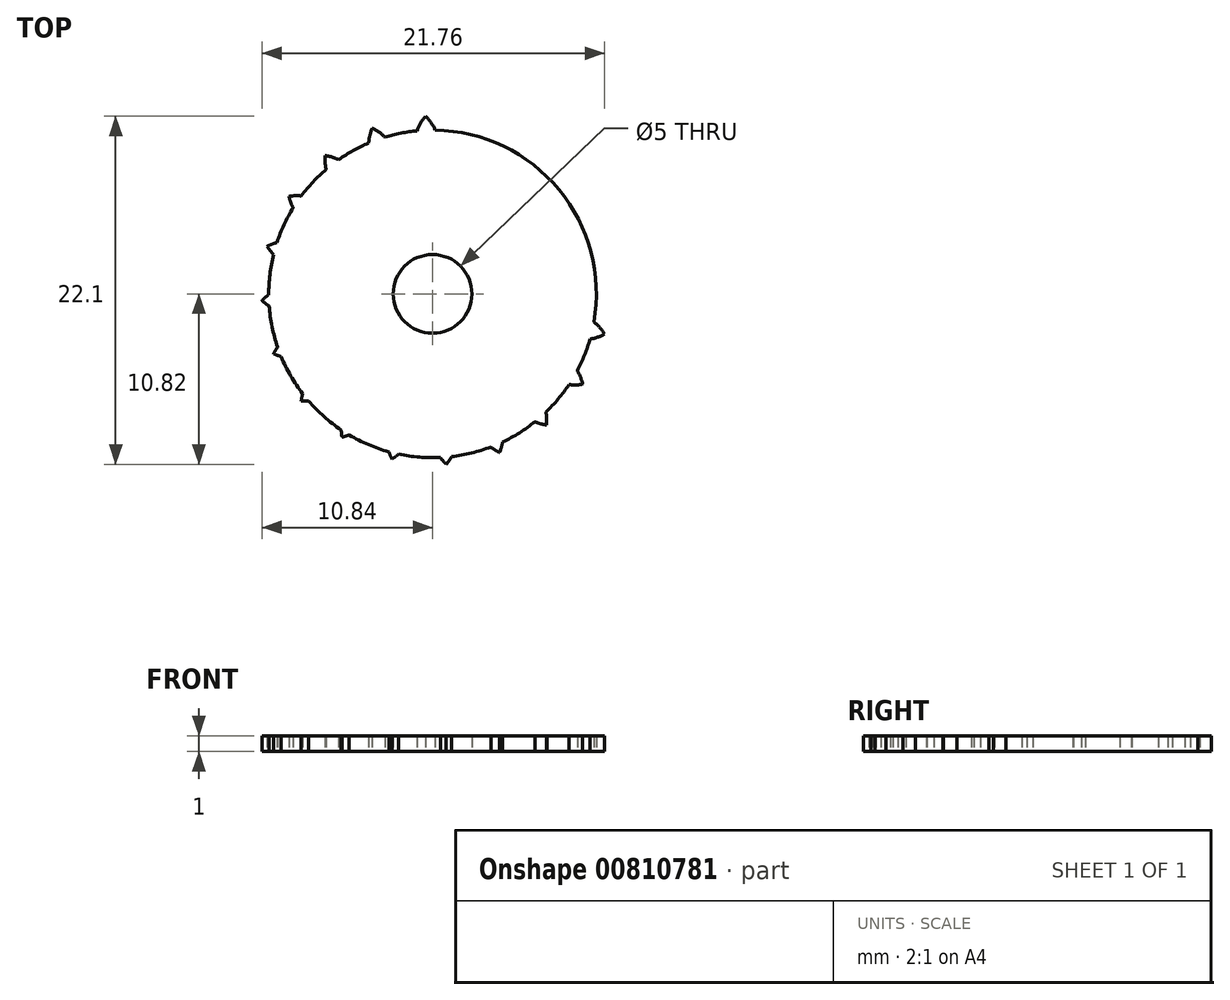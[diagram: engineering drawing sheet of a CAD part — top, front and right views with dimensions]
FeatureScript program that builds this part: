
annotation { "Feature Type Name" : "Feature", "Feature Type Description" : "" }
export const myFeature = defineFeature(function(context is Context, id is Id, definition is map)
    precondition{}
    {
        {
            assignVariable(context, id + "F0", {"name" : "GearDepth", "anyValue" : 1});
        }
        {
            var Q0;
            Q0=qCreatedBy(makeId("Top.planeOp"),FACE);
            var sketch = newSketch(context, id + "F1", { "sketchPlane" : qUnion([Q0])});
            skCircle(sketch, "E0", {"center": v(0, 0) * mm, "radius": 10.4 * mm});
            skCircle(sketch, "E1", {"center": v(0, 0) * mm, "radius": 10.95 * mm, "construction": true});
            skCircle(sketch, "E2", {"center": v(0, 0) * mm, "radius": 11.5 * mm, "construction": true});
            skLineSegment(sketch, "E3", {"start": v(0, 0) * mm, "end": v(0, 17.6) * mm, "construction": true});
            skLineSegment(sketch, "E4", {"start": v(0, 0) * mm, "end": v(-0.7, 18.04) * mm, "construction": true});
            skLineSegment(sketch, "E5", {"start": v(0, 10.95) * mm, "end": v(-10.54, 10.95) * mm, "construction": true});
            skLineSegment(sketch, "E6", {"start": v(0, 10.95) * mm, "end": v(-10.3, 7.2) * mm, "construction": true});
            skCircle(sketch, "E7", {"center": v(0, 10.95) * mm, "radius": 2.74 * mm, "construction": true});
            skCircle(sketch, "E8", {"center": v(-2.57, 10.02) * mm, "radius": 2.74 * mm, "construction": true});
            skArc(sketch, "E9", {"start": v(-5.15, 10.95) * mm, "mid": v(-5.25, 10.58) * mm, "end": v(-5.3, 10.2) * mm});
            skArc(sketch, "E10.trimOffspring", {"start": v(0.17, 10.4) * mm, "mid": v(-0.18, 11) * mm, "end": v(-0.68, 11.48) * mm});
            skArc(sketch, "E11.MirrorCS", {"start": v(-0.99, 10.36) * mm, "mid": v(-0.68, 10.98) * mm, "end": v(-0.22, 11.5) * mm});
            skLineSegment(sketch, "E12", {"start": v(-0.68, 11.48) * mm, "end": v(-0.22, 11.5) * mm});
            skArc(sketch, "E13.1.0", {"start": v(-2.97, 9.9) * mm, "mid": v(-3.5, 10.35) * mm, "end": v(-4.11, 10.65) * mm});
            skLineSegment(sketch, "E13.1.1", {"start": v(-4.11, 10.65) * mm, "end": v(-3.68, 10.81) * mm});
            skArc(sketch, "E13.1.2", {"start": v(-4.06, 9.5) * mm, "mid": v(-3.96, 10.18) * mm, "end": v(-3.68, 10.81) * mm});
            skArc(sketch, "E13.2.0", {"start": v(-5.8, 8.44) * mm, "mid": v(-6.44, 8.7) * mm, "end": v(-7.12, 8.8) * mm});
            skLineSegment(sketch, "E13.2.1", {"start": v(-7.12, 8.8) * mm, "end": v(-6.76, 9.1) * mm});
            skArc(sketch, "E13.2.2", {"start": v(-6.7, 7.72) * mm, "mid": v(-6.83, 8.4) * mm, "end": v(-6.76, 9.1) * mm});
            skArc(sketch, "E13.3.0", {"start": v(-8.04, 6.17) * mm, "mid": v(-8.73, 6.24) * mm, "end": v(-9.41, 6.12) * mm});
            skLineSegment(sketch, "E13.3.1", {"start": v(-9.41, 6.12) * mm, "end": v(-9.16, 6.5) * mm});
            skArc(sketch, "E13.3.2", {"start": v(-8.69, 5.21) * mm, "mid": v(-9, 5.83) * mm, "end": v(-9.16, 6.5) * mm});
            skArc(sketch, "E13.4.0", {"start": v(-9.48, 3.33) * mm, "mid": v(-10.15, 3.18) * mm, "end": v(-10.76, 2.86) * mm});
            skLineSegment(sketch, "E13.4.1", {"start": v(-10.76, 2.86) * mm, "end": v(-10.64, 3.3) * mm});
            skArc(sketch, "E13.4.2", {"start": v(-9.8, 2.22) * mm, "mid": v(-10.29, 2.7) * mm, "end": v(-10.64, 3.3) * mm});
            skArc(sketch, "E13.5.0", {"start": v(-9.96, 0.19) * mm, "mid": v(-10.56, -0.17) * mm, "end": v(-11.04, -0.66) * mm});
            skLineSegment(sketch, "E13.5.1", {"start": v(-11.04, -0.66) * mm, "end": v(-11.06, -0.2) * mm});
            skArc(sketch, "E13.5.2", {"start": v(-9.92, -0.97) * mm, "mid": v(-10.54, -0.66) * mm, "end": v(-11.06, -0.2) * mm});
            skArc(sketch, "E13.6.0", {"start": v(-9.45, -2.96) * mm, "mid": v(-9.9, -3.48) * mm, "end": v(-10.21, -4.1) * mm});
            skLineSegment(sketch, "E13.6.1", {"start": v(-10.21, -4.1) * mm, "end": v(-10.37, -3.66) * mm});
            skArc(sketch, "E13.6.2", {"start": v(-9.05, -4.04) * mm, "mid": v(-9.74, -3.94) * mm, "end": v(-10.37, -3.66) * mm});
            skArc(sketch, "E13.7.0", {"start": v(-8, -5.79) * mm, "mid": v(-8.27, -6.42) * mm, "end": v(-8.36, -7.1) * mm});
            skLineSegment(sketch, "E13.7.1", {"start": v(-8.36, -7.1) * mm, "end": v(-8.65, -6.74) * mm});
            skArc(sketch, "E13.7.2", {"start": v(-7.28, -6.7) * mm, "mid": v(-7.96, -6.8) * mm, "end": v(-8.65, -6.74) * mm});
            skArc(sketch, "E13.8.0", {"start": v(-5.73, -8.03) * mm, "mid": v(-5.8, -8.72) * mm, "end": v(-5.68, -9.4) * mm});
            skLineSegment(sketch, "E13.8.1", {"start": v(-5.68, -9.4) * mm, "end": v(-6.06, -9.14) * mm});
            skArc(sketch, "E13.8.2", {"start": v(-4.77, -8.67) * mm, "mid": v(-5.38, -9) * mm, "end": v(-6.06, -9.14) * mm});
            skArc(sketch, "E13.9.0", {"start": v(-2.9, -9.46) * mm, "mid": v(-2.74, -10.13) * mm, "end": v(-2.41, -10.75) * mm});
            skLineSegment(sketch, "E13.9.1", {"start": v(-2.41, -10.75) * mm, "end": v(-2.86, -10.62) * mm});
            skArc(sketch, "E13.9.2", {"start": v(-1.78, -9.77) * mm, "mid": v(-2.26, -10.27) * mm, "end": v(-2.86, -10.62) * mm});
            skArc(sketch, "E13.10.0", {"start": v(0.26, -9.94) * mm, "mid": v(0.6, -10.54) * mm, "end": v(1.1, -11.02) * mm});
            skLineSegment(sketch, "E13.10.1", {"start": v(1.1, -11.02) * mm, "end": v(0.65, -11.04) * mm});
            skArc(sketch, "E13.10.2", {"start": v(1.4, -9.9) * mm, "mid": v(1.1, -10.52) * mm, "end": v(0.65, -11.04) * mm});
            skArc(sketch, "E13.11.0", {"start": v(3.4, -9.43) * mm, "mid": v(3.92, -9.89) * mm, "end": v(4.54, -10.2) * mm});
            skLineSegment(sketch, "E13.11.1", {"start": v(4.54, -10.2) * mm, "end": v(4.1, -10.35) * mm});
            skArc(sketch, "E13.11.2", {"start": v(4.48, -9.03) * mm, "mid": v(4.38, -9.72) * mm, "end": v(4.1, -10.35) * mm});
            skArc(sketch, "E13.12.0", {"start": v(6.23, -7.98) * mm, "mid": v(6.86, -8.25) * mm, "end": v(7.55, -8.35) * mm});
            skLineSegment(sketch, "E13.12.1", {"start": v(7.55, -8.35) * mm, "end": v(7.19, -8.63) * mm});
            skArc(sketch, "E13.12.2", {"start": v(7.13, -7.26) * mm, "mid": v(7.25, -7.94) * mm, "end": v(7.19, -8.63) * mm});
            skArc(sketch, "E13.13.0", {"start": v(8.47, -5.72) * mm, "mid": v(9.16, -5.78) * mm, "end": v(9.84, -5.66) * mm});
            skLineSegment(sketch, "E13.13.1", {"start": v(9.84, -5.66) * mm, "end": v(9.58, -6.04) * mm});
            skArc(sketch, "E13.13.2", {"start": v(9.11, -4.75) * mm, "mid": v(9.43, -5.37) * mm, "end": v(9.58, -6.04) * mm});
            skArc(sketch, "E13.14.0", {"start": v(9.9, -2.87) * mm, "mid": v(10.58, -2.72) * mm, "end": v(11.19, -2.4) * mm});
            skLineSegment(sketch, "E13.14.1", {"start": v(11.19, -2.4) * mm, "end": v(11.06, -2.84) * mm});
            skArc(sketch, "E13.14.2", {"start": v(10.21, -1.76) * mm, "mid": v(10.71, -2.24) * mm, "end": v(11.06, -2.84) * mm});
            skArc(sketch, "E13.15.0", {"start": v(10.39, 0.27) * mm, "mid": v(10.98, 0.63) * mm, "end": v(11.46, 1.12) * mm});
            skLineSegment(sketch, "E13.15.1", {"start": v(11.46, 1.12) * mm, "end": v(11.48, 0.66) * mm});
            skArc(sketch, "E13.15.2", {"start": v(10.34, 1.43) * mm, "mid": v(10.96, 1.12) * mm, "end": v(11.48, 0.66) * mm});
            skArc(sketch, "E13.16.0", {"start": v(9.87, 3.41) * mm, "mid": v(10.33, 3.93) * mm, "end": v(10.64, 4.56) * mm});
            skLineSegment(sketch, "E13.16.1", {"start": v(10.64, 4.56) * mm, "end": v(10.8, 4.12) * mm});
            skArc(sketch, "E13.16.2", {"start": v(9.47, 4.5) * mm, "mid": v(10.16, 4.4) * mm, "end": v(10.8, 4.12) * mm});
            skArc(sketch, "E13.17.0", {"start": v(8.42, 6.24) * mm, "mid": v(8.7, 6.88) * mm, "end": v(8.79, 7.57) * mm});
            skLineSegment(sketch, "E13.17.1", {"start": v(8.79, 7.57) * mm, "end": v(9.07, 7.2) * mm});
            skArc(sketch, "E13.17.2", {"start": v(7.7, 7.15) * mm, "mid": v(8.38, 7.27) * mm, "end": v(9.07, 7.2) * mm});
            skArc(sketch, "E13.18.0", {"start": v(6.16, 8.49) * mm, "mid": v(6.22, 9.17) * mm, "end": v(6.1, 9.86) * mm});
            skLineSegment(sketch, "E13.18.1", {"start": v(6.1, 9.86) * mm, "end": v(6.49, 9.6) * mm});
            skArc(sketch, "E13.18.2", {"start": v(5.2, 9.13) * mm, "mid": v(5.8, 9.45) * mm, "end": v(6.49, 9.6) * mm});
            skArc(sketch, "E13.19.0", {"start": v(3.32, 9.92) * mm, "mid": v(3.16, 10.6) * mm, "end": v(2.84, 11.2) * mm});
            skLineSegment(sketch, "E13.19.1", {"start": v(2.84, 11.2) * mm, "end": v(3.28, 11.08) * mm});
            skArc(sketch, "E13.19.2", {"start": v(2.2, 10.23) * mm, "mid": v(2.69, 10.73) * mm, "end": v(3.28, 11.08) * mm});
            skPoint(sketch, "E13.center", {"position": v(0.21, 0.23) * mm});
            skCircle(sketch, "E14", {"center": v(0, 0) * mm, "radius": 2.5 * mm});
            skSolve(sketch);
        }
        {
            var Q0;
            {var subQ0=sQuery(id+"F1.wireOp",EDGE,"E10.trimOffspring");Q0=makeQuery(id+"F1.imprint","IMPRINT",FACE,{"disambiguationData":[TD([[makeQuery(id+"F1.imprint","IMPRINT",EDGE,{"derivedFrom":subQ0}),1.0]])]});}
            var Q1;
            {var subQ0=sQuery(id+"F1.wireOp",EDGE,"E0");var subQ1=makeQuery(id+"F1.imprint","INTERSECT",VERTEX,{"derivedFrom":[subQ0,sQuery(id+"F1.wireOp",EDGE,"E10.trimOffspring")]});Q1=makeQuery(id+"F1.imprint","IMPRINT",FACE,{"disambiguationData":[TD([[makeQuery(id+"F1.imprint","IMPRINT",EDGE,{"disambiguationData":[TD([[subQ1,-1.0]])],"derivedFrom":subQ0}),1.0]])]});}
            var Q2;
            {var subQ0=sQuery(id+"F1.wireOp",EDGE,"E13.1.0");Q2=makeQuery(id+"F1.imprint","IMPRINT",FACE,{"disambiguationData":[TD([[makeQuery(id+"F1.imprint","IMPRINT",EDGE,{"derivedFrom":subQ0}),1.0]])]});}
            var Q3;
            {var subQ0=sQuery(id+"F1.wireOp",EDGE,"E13.2.0");Q3=makeQuery(id+"F1.imprint","IMPRINT",FACE,{"disambiguationData":[TD([[makeQuery(id+"F1.imprint","IMPRINT",EDGE,{"derivedFrom":subQ0}),1.0]])]});}
            var Q4;
            {var subQ0=sQuery(id+"F1.wireOp",EDGE,"E13.3.0");Q4=makeQuery(id+"F1.imprint","IMPRINT",FACE,{"disambiguationData":[TD([[makeQuery(id+"F1.imprint","IMPRINT",EDGE,{"derivedFrom":subQ0}),1.0]])]});}
            var Q5;
            {var subQ0=sQuery(id+"F1.wireOp",EDGE,"E13.4.0");Q5=makeQuery(id+"F1.imprint","IMPRINT",FACE,{"disambiguationData":[TD([[makeQuery(id+"F1.imprint","IMPRINT",EDGE,{"derivedFrom":subQ0}),1.0]])]});}
            var Q6;
            {var subQ0=sQuery(id+"F1.wireOp",EDGE,"E13.5.0");Q6=makeQuery(id+"F1.imprint","IMPRINT",FACE,{"disambiguationData":[TD([[makeQuery(id+"F1.imprint","IMPRINT",EDGE,{"derivedFrom":subQ0}),1.0]])]});}
            var Q7;
            {var subQ0=sQuery(id+"F1.wireOp",EDGE,"E13.6.0");Q7=makeQuery(id+"F1.imprint","IMPRINT",FACE,{"disambiguationData":[TD([[makeQuery(id+"F1.imprint","IMPRINT",EDGE,{"derivedFrom":subQ0}),1.0]])]});}
            var Q8;
            {var subQ0=sQuery(id+"F1.wireOp",EDGE,"E13.7.0");Q8=makeQuery(id+"F1.imprint","IMPRINT",FACE,{"disambiguationData":[TD([[makeQuery(id+"F1.imprint","IMPRINT",EDGE,{"derivedFrom":subQ0}),1.0]])]});}
            var Q9;
            {var subQ0=sQuery(id+"F1.wireOp",EDGE,"E13.8.0");Q9=makeQuery(id+"F1.imprint","IMPRINT",FACE,{"disambiguationData":[TD([[makeQuery(id+"F1.imprint","IMPRINT",EDGE,{"derivedFrom":subQ0}),1.0]])]});}
            var Q10;
            {var subQ0=sQuery(id+"F1.wireOp",EDGE,"E13.9.0");Q10=makeQuery(id+"F1.imprint","IMPRINT",FACE,{"disambiguationData":[TD([[makeQuery(id+"F1.imprint","IMPRINT",EDGE,{"derivedFrom":subQ0}),1.0]])]});}
            var Q11;
            {var subQ0=sQuery(id+"F1.wireOp",EDGE,"E13.10.0");Q11=makeQuery(id+"F1.imprint","IMPRINT",FACE,{"disambiguationData":[TD([[makeQuery(id+"F1.imprint","IMPRINT",EDGE,{"derivedFrom":subQ0}),1.0]])]});}
            var Q12;
            {var subQ0=sQuery(id+"F1.wireOp",EDGE,"E13.11.0");Q12=makeQuery(id+"F1.imprint","IMPRINT",FACE,{"disambiguationData":[TD([[makeQuery(id+"F1.imprint","IMPRINT",EDGE,{"derivedFrom":subQ0}),1.0]])]});}
            var Q13;
            {var subQ0=sQuery(id+"F1.wireOp",EDGE,"E13.12.0");Q13=makeQuery(id+"F1.imprint","IMPRINT",FACE,{"disambiguationData":[TD([[makeQuery(id+"F1.imprint","IMPRINT",EDGE,{"derivedFrom":subQ0}),1.0]])]});}
            var Q14;
            {var subQ0=sQuery(id+"F1.wireOp",EDGE,"E13.13.0");Q14=makeQuery(id+"F1.imprint","IMPRINT",FACE,{"disambiguationData":[TD([[makeQuery(id+"F1.imprint","IMPRINT",EDGE,{"derivedFrom":subQ0}),1.0]])]});}
            var Q15;
            {var subQ0=sQuery(id+"F1.wireOp",EDGE,"E13.14.0");Q15=makeQuery(id+"F1.imprint","IMPRINT",FACE,{"disambiguationData":[TD([[makeQuery(id+"F1.imprint","IMPRINT",EDGE,{"derivedFrom":subQ0}),1.0]])]});}
            var Q16;
            {var subQ0=sQuery(id+"F1.wireOp",EDGE,"E13.15.0");Q16=makeQuery(id+"F1.imprint","IMPRINT",FACE,{"disambiguationData":[TD([[makeQuery(id+"F1.imprint","IMPRINT",EDGE,{"derivedFrom":subQ0}),1.0]])]});}
            var Q17;
            {var subQ0=sQuery(id+"F1.wireOp",EDGE,"E13.16.0");Q17=makeQuery(id+"F1.imprint","IMPRINT",FACE,{"disambiguationData":[TD([[makeQuery(id+"F1.imprint","IMPRINT",EDGE,{"derivedFrom":subQ0}),1.0]])]});}
            var Q18;
            {var subQ0=sQuery(id+"F1.wireOp",EDGE,"E13.17.0");Q18=makeQuery(id+"F1.imprint","IMPRINT",FACE,{"disambiguationData":[TD([[makeQuery(id+"F1.imprint","IMPRINT",EDGE,{"derivedFrom":subQ0}),1.0]])]});}
            var Q19;
            {var subQ0=sQuery(id+"F1.wireOp",EDGE,"E13.18.0");Q19=makeQuery(id+"F1.imprint","IMPRINT",FACE,{"disambiguationData":[TD([[makeQuery(id+"F1.imprint","IMPRINT",EDGE,{"derivedFrom":subQ0}),1.0]])]});}
            var Q20;
            {var subQ0=sQuery(id+"F1.wireOp",EDGE,"E13.19.0");Q20=makeQuery(id+"F1.imprint","IMPRINT",FACE,{"disambiguationData":[TD([[makeQuery(id+"F1.imprint","IMPRINT",EDGE,{"derivedFrom":subQ0}),1.0]])]});}
            var Q21;
            Q21=sQuery(id+"F1.wireOp",EDGE,"E0");
            var Q22;
            Q22=sQuery(id+"F1.wireOp",EDGE,"E10.trimOffspring");
            var Q23;
            Q23=sQuery(id+"F1.wireOp",EDGE,"E12");
            var Q24;
            Q24=sQuery(id+"F1.wireOp",EDGE,"E11.MirrorCS");
            extrude(context, id + "F2", {"entities" : qUnion([Q0, Q1, Q2, Q3, Q4, Q5, Q6, Q7, Q8, Q9, Q10, Q11, Q12, Q13, Q14, Q15, Q16, Q17, Q18, Q19, Q20]), "surfaceEntities" : qUnion([Q21, Q22, Q23, Q24]), "depth" : (getVariable(context, 'GearDepth')) * mm});
        }
    });
